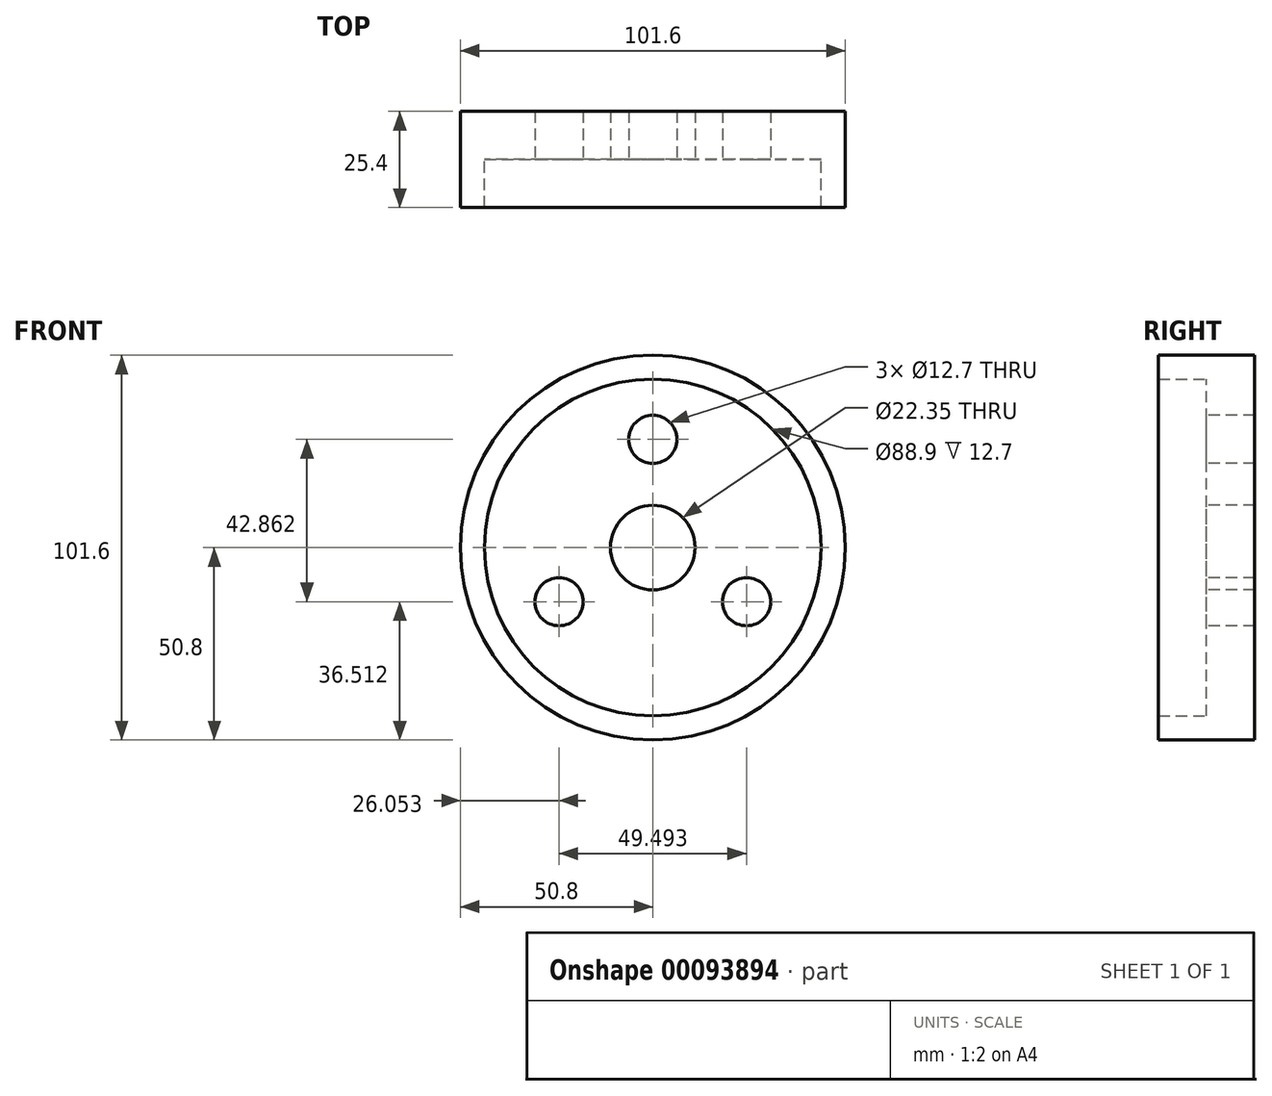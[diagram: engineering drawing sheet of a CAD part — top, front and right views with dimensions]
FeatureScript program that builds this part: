
annotation { "Feature Type Name" : "Feature", "Feature Type Description" : "" }
export const myFeature = defineFeature(function(context is Context, id is Id, definition is map)
    precondition{}
    {
        {
            var Q0;
            Q0=qCreatedBy(makeId("Front.planeOp"),FACE);
            var sketch = newSketch(context, id + "F0", { "sketchPlane" : qUnion([Q0])});
            skCircle(sketch, "E0", {"center": v(0, 0) * mm, "radius": 50.8 * mm});
            skCircle(sketch, "E1", {"center": v(0, 0) * mm, "radius": 44.45 * mm});
            skCircle(sketch, "E2", {"center": v(0, 0) * mm, "radius": 11.18 * mm});
            skCircle(sketch, "E3", {"center": v(0, 0) * mm, "radius": 28.58 * mm, "construction": true});
            skSolve(sketch);
        }
        {
            var Q0;
            Q0=makeQuery(id+"F0.imprint","IMPRINT",FACE,{"disambiguationData":[TD([[makeQuery(id+"F0.imprint","IMPRINT",EDGE,{"derivedFrom":sQuery(id+"F0.wireOp",EDGE,"E0")}),1.0]])]});
            var Q1;
            Q1=makeQuery(id+"F0.imprint","IMPRINT",FACE,{"disambiguationData":[TD([[makeQuery(id+"F0.imprint","IMPRINT",EDGE,{"derivedFrom":sQuery(id+"F0.wireOp",EDGE,"E1")}),1.0]])]});
            var Q2;
            Q2=makeQuery(id+"F0.imprint","IMPRINT",FACE,{"disambiguationData":[TD([[makeQuery(id+"F0.imprint","IMPRINT",EDGE,{"derivedFrom":sQuery(id+"F0.wireOp",EDGE,"E2")}),1.0]])]});
            extrude(context, id + "F1", {"entities" : qUnion([Q0, Q1, Q2]), "depth" : 12.7 * mm});
        }
        {
            var Q0;
            Q0=makeQuery(id+"F1.opExtrude","CAP_FACE",FACE,{"disambiguationData":[OSD([sQuery(id+"F0.wireOp",EDGE,"E0")])],"isStart":false});
            var sketch = newSketch(context, id + "F2", { "sketchPlane" : qUnion([Q0])});
            skCircle(sketch, "E4.0", {"center": v(0, 0) * mm, "radius": 11.18 * mm});
            skCircle(sketch, "E5.0", {"center": v(0, 0) * mm, "radius": 28.58 * mm, "construction": true});
            skCircle(sketch, "E6.0", {"center": v(0, 0) * mm, "radius": 44.45 * mm});
            skCircle(sketch, "E7", {"center": v(0, 28.58) * mm, "radius": 6.35 * mm});
            skCircle(sketch, "E8.1.0", {"center": v(-24.75, -14.29) * mm, "radius": 6.35 * mm});
            skCircle(sketch, "E8.2.0", {"center": v(24.75, -14.29) * mm, "radius": 6.35 * mm});
            skSolve(sketch);
        }
        {
            var Q0;
            {var subQ0=sQuery(id+"F2.wireOp",EDGE,"E8.2.0");var subQ1=sQuery(id+"F2.wireOp",EDGE,"IYkEUhcQ-mvZO-FufO-YCzK-C6hryyUaip1n");var subQ2=makeQuery(id+"F2.imprint","INTERSECT",VERTEX,{"disambiguationData":[OD(0.0)],"derivedFrom":[subQ1,subQ0]});Q0=makeQuery(id+"F2.imprint","IMPRINT",FACE,{"disambiguationData":[TD([[makeQuery(id+"F2.imprint","IMPRINT",EDGE,{"disambiguationData":[TD([[subQ2,-1.0]])],"derivedFrom":subQ1}),1.0]])]});}
            var Q1;
            Q1=makeQuery(id+"F2.imprint","IMPRINT",FACE,{"disambiguationData":[TD([[makeQuery(id+"F2.imprint","IMPRINT",EDGE,{"derivedFrom":sQuery(id+"F2.wireOp",EDGE,"E7")}),1.0]])]});
            var Q2;
            Q2=makeQuery(id+"F2.imprint","IMPRINT",FACE,{"disambiguationData":[TD([[makeQuery(id+"F2.imprint","IMPRINT",EDGE,{"derivedFrom":sQuery(id+"F2.wireOp",EDGE,"E8.1.0")}),1.0]])]});
            var Q3;
            Q3=makeQuery(id+"F2.imprint","IMPRINT",FACE,{"disambiguationData":[TD([[makeQuery(id+"F2.imprint","IMPRINT",EDGE,{"derivedFrom":sQuery(id+"F2.wireOp",EDGE,"E4.0")}),1.0]])]});
            var Q4;
            Q4=makeQuery(id+"F2.imprint","IMPRINT",FACE,{"disambiguationData":[TD([[makeQuery(id+"F2.imprint","IMPRINT",EDGE,{"derivedFrom":sQuery(id+"F2.wireOp",EDGE,"E8.2.0")}),1.0]])]});
            extrude(context, id + "F3", {"entities" : qUnion([Q0, Q1, Q2, Q3, Q4]), "operationType" : NewBodyOperationType.REMOVE, "endBound" : BoundingType.THROUGH_ALL, "oppositeDirection" : true, "depth" : 25.4 * mm});
        }
        {
            var Q0;
            Q0=makeQuery(id+"F2.imprint","IMPRINT",FACE,{"disambiguationData":[TD([[makeQuery(id+"F2.imprint","IMPRINT",EDGE,{"derivedFrom":sQuery(id+"F2.wireOp",EDGE,"E6.0")}),-1.0]])]});
            extrude(context, id + "F4", {"entities" : qUnion([Q0]), "operationType" : NewBodyOperationType.ADD, "depth" : 12.7 * mm});
        }
    });
